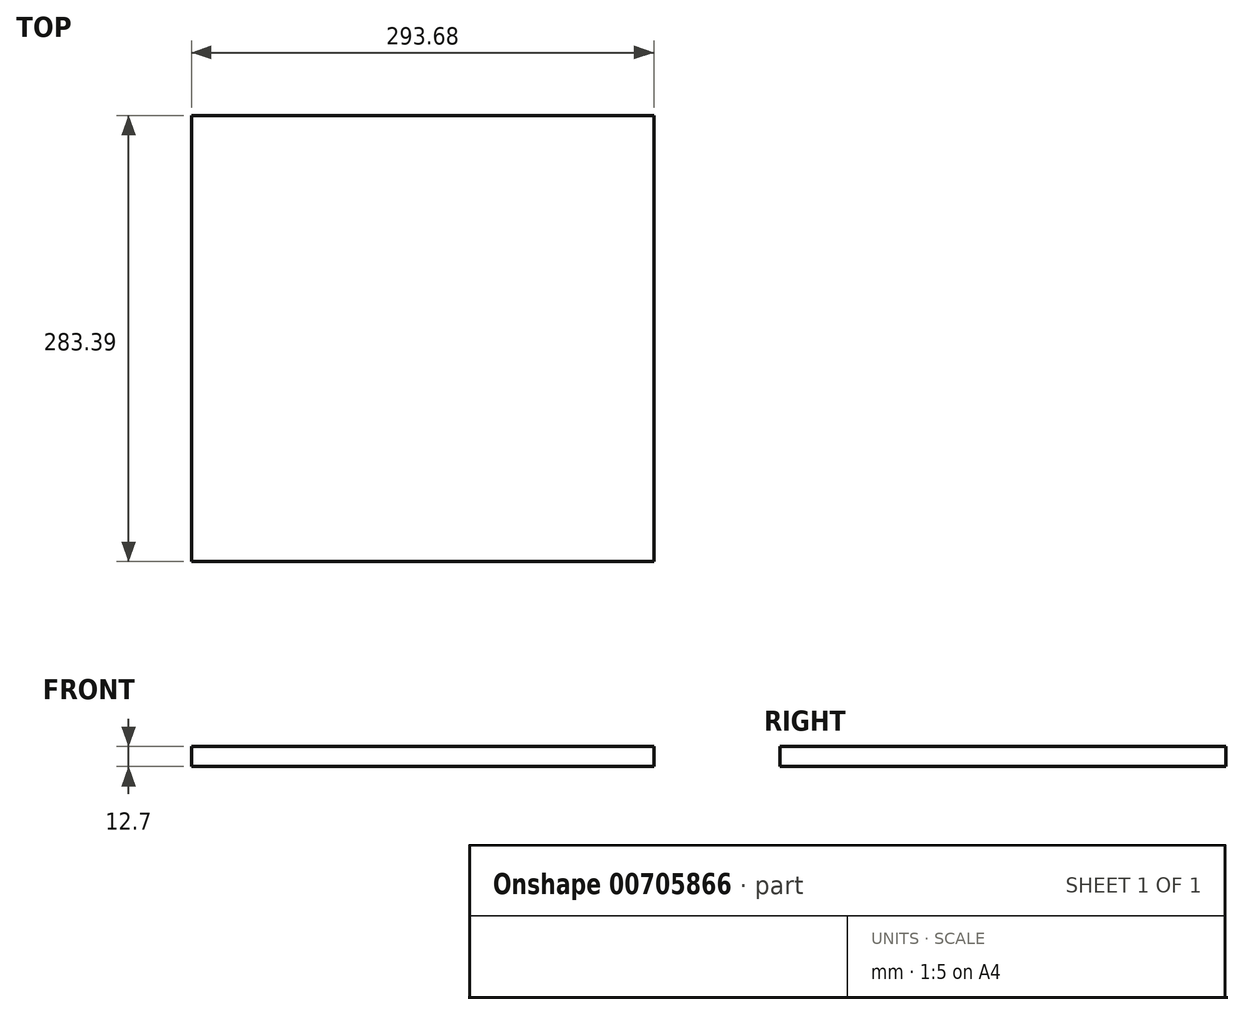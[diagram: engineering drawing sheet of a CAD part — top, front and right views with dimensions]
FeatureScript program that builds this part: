
annotation { "Feature Type Name" : "Feature", "Feature Type Description" : "" }
export const myFeature = defineFeature(function(context is Context, id is Id, definition is map)
    precondition{}
    {
        {
            var Q0;
            Q0=qCreatedBy(makeId("Top.planeOp"),FACE);
            var sketch = newSketch(context, id + "F0", { "sketchPlane" : qUnion([Q0])});
            skLineSegment(sketch, "E0.bottom", {"start": v(146.84, 135.18) * mm, "end": v(-146.84, 135.18) * mm});
            skLineSegment(sketch, "E0.top", {"start": v(146.84, -148.21) * mm, "end": v(-146.84, -148.21) * mm});
            skLineSegment(sketch, "E0.left", {"start": v(146.84, 135.18) * mm, "end": v(146.84, -148.21) * mm});
            skLineSegment(sketch, "E0.right", {"start": v(-146.84, 135.18) * mm, "end": v(-146.84, -148.21) * mm});
            skPoint(sketch, "E0.middle", {"position": v(0, -6.52) * mm});
            skSolve(sketch);
        }
        {
            var Q0;
            Q0=makeQuery(id+"F0.imprint","IMPRINT",FACE,{"disambiguationData":[TD([[makeQuery(id+"F0.imprint","IMPRINT",EDGE,{"derivedFrom":sQuery(id+"F0.wireOp",EDGE,"E0.bottom")}),1.0]])]});
            extrude(context, id + "F1", {"entities" : qUnion([Q0]), "oppositeDirection" : true, "depth" : 12.7 * mm, "offsetDistance" : 25.4 * mm});
        }
    });
